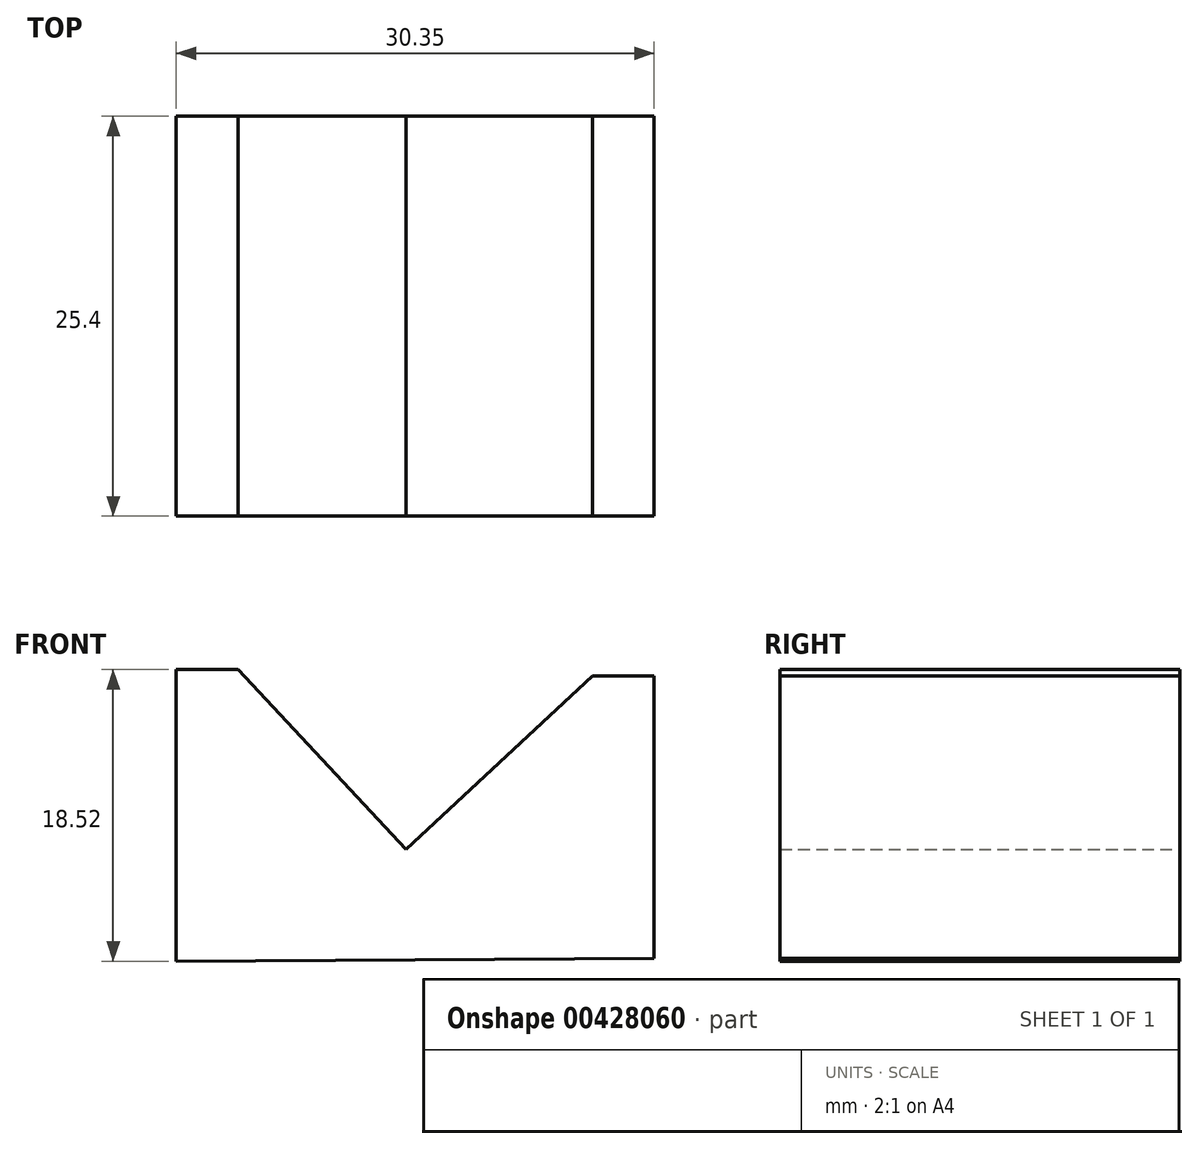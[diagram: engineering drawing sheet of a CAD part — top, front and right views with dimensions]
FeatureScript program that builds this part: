
annotation { "Feature Type Name" : "Feature", "Feature Type Description" : "" }
export const myFeature = defineFeature(function(context is Context, id is Id, definition is map)
    precondition{}
    {
        {
            var Q0;
            Q0=qCreatedBy(makeId("Front.planeOp"),FACE);
            var sketch = newSketch(context, id + "F0", { "sketchPlane" : qUnion([Q0])});
            skLineSegment(sketch, "E0", {"start": v(-55.97, -39.41) * mm, "end": v(-55.97, -20.89) * mm});
            skLineSegment(sketch, "E1", {"start": v(-55.97, -20.89) * mm, "end": v(-52.03, -20.89) * mm});
            skLineSegment(sketch, "E2", {"start": v(-52.03, -20.89) * mm, "end": v(-41.38, -32.32) * mm});
            skLineSegment(sketch, "E3", {"start": v(-41.38, -32.32) * mm, "end": v(-29.55, -21.3) * mm});
            skLineSegment(sketch, "E4", {"start": v(-29.55, -21.3) * mm, "end": v(-25.62, -21.3) * mm});
            skLineSegment(sketch, "E5", {"start": v(-25.62, -21.3) * mm, "end": v(-25.62, -39.22) * mm});
            skLineSegment(sketch, "E6", {"start": v(-25.62, -39.22) * mm, "end": v(-55.97, -39.41) * mm});
            skSolve(sketch);
        }
        {
            var Q0;
            Q0 = qSketchRegion(id + "F0", true);
            extrude(context, id + "F1", {"entities" : qUnion([Q0]), "depth" : 25.4 * mm, "offsetDistance" : 25.4 * mm});
        }
    });
